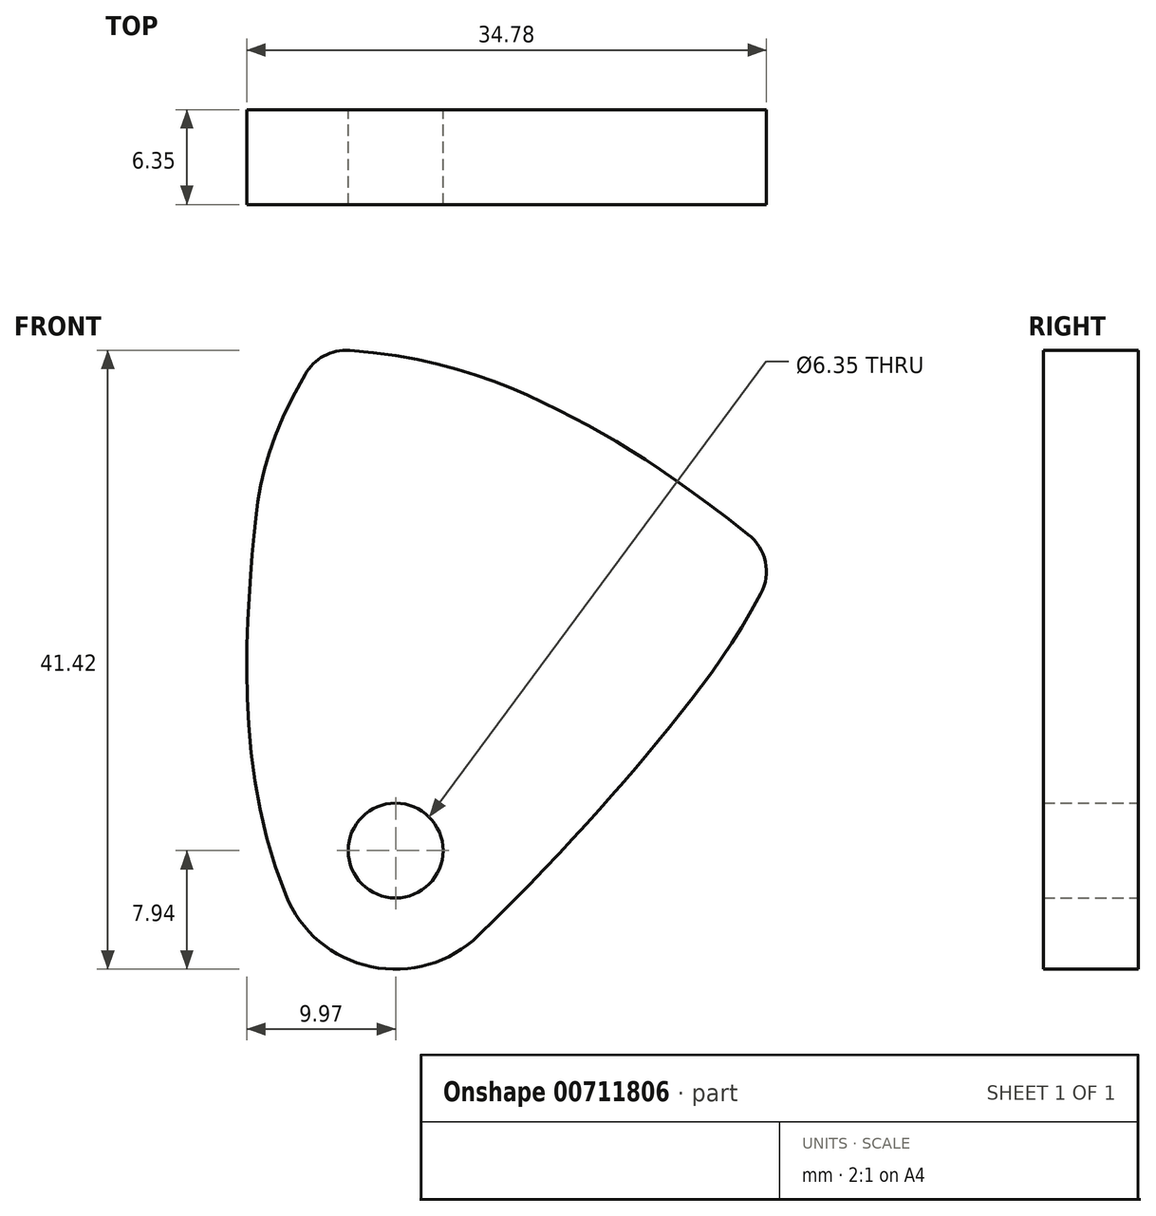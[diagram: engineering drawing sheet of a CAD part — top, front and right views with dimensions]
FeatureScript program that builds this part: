
annotation { "Feature Type Name" : "Feature", "Feature Type Description" : "" }
export const myFeature = defineFeature(function(context is Context, id is Id, definition is map)
    precondition{}
    {
        {
            var Q0;
            Q0=qCreatedBy(makeId("Front.planeOp"),FACE);
            var sketch = newSketch(context, id + "F0", { "sketchPlane" : qUnion([Q0])});
            skCircle(sketch, "E0", {"center": v(0, 0) * mm, "radius": 3.18 * mm});
            skArc(sketch, "E1", {"start": v(-7.37, -2.96) * mm, "mid": v(-1.64, -7.77) * mm, "end": v(5.55, -5.68) * mm});
            skArc(sketch, "E2", {"start": v(24.44, 17.17) * mm, "mid": v(24.74, 19.33) * mm, "end": v(23.59, 21.17) * mm});
            skArc(sketch, "E3", {"start": v(-3.07, 33.47) * mm, "mid": v(-4.8, 33.1) * mm, "end": v(-6.06, 31.85) * mm});
            skFitSpline(sketch, "E4", {"points": [v(-3.07, 33.47) * mm, v(11.55, 29.15) * mm, v(23.59, 21.17) * mm], "startDerivative": vector(37.12, -2.52) * mm, "endDerivative": vector(31.49, -24.5) * mm});
            skFitSpline(sketch, "E5", {"points": [v(26.65, 21.96) * mm, v(18.17, 8.07) * mm, v(5.55, -5.68) * mm], "startDerivative": vector(-15.38, -38.48) * mm, "endDerivative": vector(-32.17, -31.45) * mm});
            skFitSpline(sketch, "E6", {"points": [v(-6.06, 31.85) * mm, v(-9.55, 20.28) * mm, v(-7.37, -2.96) * mm], "startDerivative": vector(-20.45, -36.5) * mm, "endDerivative": vector(17.38, -43.32) * mm});
            skSolve(sketch);
        }
        {
            var Q0;
            Q0 = qSketchRegion(id + "F0", true);
            extrude(context, id + "F1", {"entities" : qUnion([Q0]), "depth" : 6.35 * mm, "offsetDistance" : 25.4 * mm});
        }
    });
